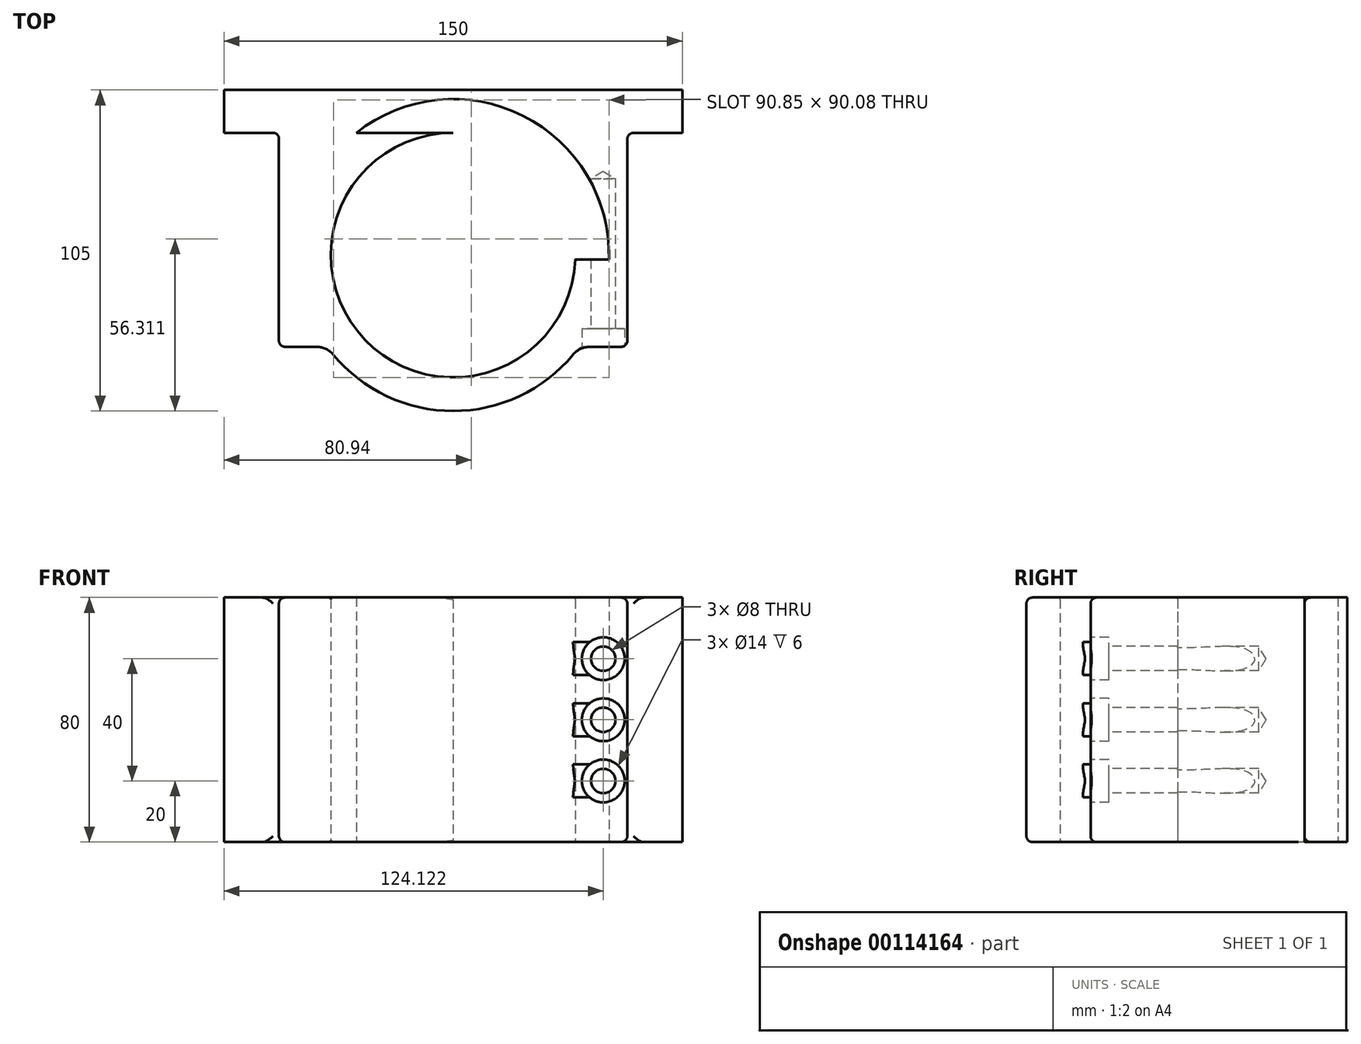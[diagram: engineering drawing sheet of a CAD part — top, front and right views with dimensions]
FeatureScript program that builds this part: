
annotation { "Feature Type Name" : "Feature", "Feature Type Description" : "" }
export const myFeature = defineFeature(function(context is Context, id is Id, definition is map)
    precondition{}
    {
        {
            var Q0;
            Q0=qCreatedBy(makeId("Top.planeOp"),FACE);
            var sketch = newSketch(context, id + "F0", { "sketchPlane" : qUnion([Q0])});
            skCircle(sketch, "E0", {"center": v(0, -54) * mm, "radius": 40 * mm});
            skCircle(sketch, "E1", {"center": v(0, -54) * mm, "radius": 51 * mm});
            skLineSegment(sketch, "E2", {"start": v(0, 0) * mm, "end": v(0, -54) * mm, "construction": true});
            skLineSegment(sketch, "E3", {"start": v(0, -54) * mm, "end": v(40, -54) * mm, "construction": true});
            skLineSegment(sketch, "E4", {"start": v(40, -54) * mm, "end": v(51, -54) * mm, "construction": true});
            skLineSegment(sketch, "E5.bottom", {"start": v(75, -14) * mm, "end": v(-75, -14) * mm});
            skLineSegment(sketch, "E5.top", {"start": v(75, 0) * mm, "end": v(-75, 0) * mm});
            skLineSegment(sketch, "E5.left", {"start": v(75, -14) * mm, "end": v(75, 0) * mm});
            skLineSegment(sketch, "E5.right", {"start": v(-75, -14) * mm, "end": v(-75, 0) * mm});
            skPoint(sketch, "E5.middle", {"position": v(0, -7) * mm});
            skLineSegment(sketch, "E6.bottom", {"start": v(57, -84) * mm, "end": v(-57, -84) * mm});
            skLineSegment(sketch, "E6.top", {"start": v(57, -14) * mm, "end": v(-57, -14) * mm});
            skLineSegment(sketch, "E6.left", {"start": v(57, -84) * mm, "end": v(57, -14) * mm});
            skLineSegment(sketch, "E6.right", {"start": v(-57, -84) * mm, "end": v(-57, -14) * mm});
            skPoint(sketch, "E6.middle", {"position": v(0, -49) * mm});
            skLineSegment(sketch, "E7.bottom", {"start": v(57, -55.5) * mm, "end": v(34, -55.5) * mm});
            skLineSegment(sketch, "E7.top", {"start": v(57, -52.5) * mm, "end": v(34, -52.5) * mm});
            skLineSegment(sketch, "E7.left", {"start": v(57, -55.5) * mm, "end": v(57, -52.5) * mm});
            skLineSegment(sketch, "E7.right", {"start": v(34, -55.5) * mm, "end": v(34, -52.5) * mm});
            skPoint(sketch, "E7.middle", {"position": v(45.5, -54) * mm});
            skLineSegment(sketch, "E8", {"start": v(0, -54) * mm, "end": v(0, -105) * mm, "construction": true});
            skSolve(sketch);
        }
        {
            var Q0;
            {var subQ0=sQuery(id+"F0.wireOp",EDGE,"E5.right");Q0=makeQuery(id+"F0.imprint","IMPRINT",FACE,{"disambiguationData":[TD([[makeQuery(id+"F0.imprint","IMPRINT",EDGE,{"derivedFrom":subQ0}),-1.0]])]});}
            var Q1;
            {var subQ5=sQuery(id+"F0.wireOp",EDGE,"E6.right");Q1=makeQuery(id+"F0.imprint","IMPRINT",FACE,{"disambiguationData":[TD([[makeQuery(id+"F0.imprint","IMPRINT",EDGE,{"derivedFrom":subQ5}),-1.0]])]});}
            var Q2;
            {var subQ0=sQuery(id+"F0.wireOp",EDGE,"E6.top");var subQ1=sQuery(id+"F0.wireOp",EDGE,"E0");var subQ7=makeQuery(id+"F0.imprint","INTERSECT",VERTEX,{"disambiguationData":[OD(0.0)],"derivedFrom":[subQ1,subQ0]});Q2=makeQuery(id+"F0.imprint","IMPRINT",FACE,{"disambiguationData":[TD([[makeQuery(id+"F0.imprint","IMPRINT",EDGE,{"disambiguationData":[TD([[subQ7,1.0]])],"derivedFrom":subQ1}),-1.0]])]});}
            var Q3;
            {var subQ0=sQuery(id+"F0.wireOp",EDGE,"E6.top");var subQ1=sQuery(id+"F0.wireOp",EDGE,"E0");var subQ2=makeQuery(id+"F0.imprint","INTERSECT",VERTEX,{"disambiguationData":[OD(0.0)],"derivedFrom":[subQ1,subQ0]});Q3=makeQuery(id+"F0.imprint","IMPRINT",FACE,{"disambiguationData":[TD([[makeQuery(id+"F0.imprint","IMPRINT",EDGE,{"disambiguationData":[TD([[subQ2,-1.0]])],"derivedFrom":subQ1}),-1.0]])]});}
            var Q4;
            {var subQ0=sQuery(id+"F0.wireOp",EDGE,"E5.left");Q4=makeQuery(id+"F0.imprint","IMPRINT",FACE,{"disambiguationData":[TD([[makeQuery(id+"F0.imprint","IMPRINT",EDGE,{"derivedFrom":subQ0}),1.0]])]});}
            var Q5;
            {var subQ5=sQuery(id+"F0.wireOp",EDGE,"E6.left");Q5=makeQuery(id+"F0.imprint","IMPRINT",FACE,{"disambiguationData":[TD([[makeQuery(id+"F0.imprint","IMPRINT",EDGE,{"derivedFrom":subQ5}),1.0]])]});}
            var Q6;
            {var subQ0=sQuery(id+"F0.wireOp",EDGE,"E6.top");var subQ1=sQuery(id+"F0.wireOp",EDGE,"E0");var subQ2=makeQuery(id+"F0.imprint","INTERSECT",VERTEX,{"disambiguationData":[OD(1.0)],"derivedFrom":[subQ1,subQ0]});Q6=makeQuery(id+"F0.imprint","IMPRINT",FACE,{"disambiguationData":[TD([[makeQuery(id+"F0.imprint","IMPRINT",EDGE,{"disambiguationData":[TD([[subQ2,1.0]])],"derivedFrom":subQ1}),-1.0]])]});}
            var Q7;
            {var subQ0=sQuery(id+"F0.wireOp",EDGE,"E6.bottom");var subQ1=sQuery(id+"F0.wireOp",EDGE,"E0");var subQ2=makeQuery(id+"F0.imprint","INTERSECT",VERTEX,{"disambiguationData":[OD(0.0)],"derivedFrom":[subQ1,subQ0]});Q7=makeQuery(id+"F0.imprint","IMPRINT",FACE,{"disambiguationData":[TD([[makeQuery(id+"F0.imprint","IMPRINT",EDGE,{"disambiguationData":[TD([[subQ2,-1.0]])],"derivedFrom":subQ1}),-1.0]])]});}
            var Q8;
            {var subQ0=sQuery(id+"F0.wireOp",EDGE,"E6.bottom");var subQ1=sQuery(id+"F0.wireOp",EDGE,"E0");var subQ2=makeQuery(id+"F0.imprint","INTERSECT",VERTEX,{"disambiguationData":[OD(1.0)],"derivedFrom":[subQ1,subQ0]});Q8=makeQuery(id+"F0.imprint","IMPRINT",FACE,{"disambiguationData":[TD([[makeQuery(id+"F0.imprint","IMPRINT",EDGE,{"disambiguationData":[TD([[subQ2,-1.0]])],"derivedFrom":subQ1}),-1.0]])]});}
            var Q9;
            {var subQ0=sQuery(id+"F0.wireOp",EDGE,"E6.top");var subQ1=sQuery(id+"F0.wireOp",EDGE,"E0");var subQ2=makeQuery(id+"F0.imprint","INTERSECT",VERTEX,{"disambiguationData":[OD(1.0)],"derivedFrom":[subQ1,subQ0]});Q9=makeQuery(id+"F0.imprint","IMPRINT",FACE,{"disambiguationData":[TD([[makeQuery(id+"F0.imprint","IMPRINT",EDGE,{"disambiguationData":[TD([[subQ2,-1.0]])],"derivedFrom":subQ1}),-1.0]])]});}
            var Q10;
            {var subQ0=sQuery(id+"F0.wireOp",EDGE,"E6.top");var subQ1=sQuery(id+"F0.wireOp",EDGE,"E1");var subQ2=makeQuery(id+"F0.imprint","INTERSECT",VERTEX,{"disambiguationData":[OD(0.0)],"derivedFrom":[subQ1,subQ0]});Q10=makeQuery(id+"F0.imprint","IMPRINT",FACE,{"disambiguationData":[TD([[makeQuery(id+"F0.imprint","IMPRINT",EDGE,{"disambiguationData":[TD([[subQ2,-1.0]])],"derivedFrom":subQ1}),1.0]])]});}
            extrude(context, id + "F1", {"entities" : qUnion([Q0, Q1, Q2, Q3, Q4, Q5, Q6, Q7, Q8, Q9, Q10]), "depth" : 80 * mm});
        }
        {
            var Q0;
            {var subQ0=sQuery(id+"F0.wireOp",EDGE,"E6.bottom");Q0=makeQuery(id+"F1.opExtrude","SWEPT_FACE",FACE,{"disambiguationData":[OSD([subQ0]),TDD([makeQuery(id+"F0.imprint","IMPRINT",EDGE,{"disambiguationData":[TD([[makeQuery(id+"F0.imprint","INTERSECT",VERTEX,{"derivedFrom":[subQ0,sQuery(id+"F0.wireOp",EDGE,"E6.left")]}),-1.0]])],"derivedFrom":subQ0})])]});}
            var sketch = newSketch(context, id + "F2", { "sketchPlane" : qUnion([Q0])});
            skLineSegment(sketch, "E9", {"start": v(49.12, 0) * mm, "end": v(49.12, 20) * mm, "construction": true});
            skLineSegment(sketch, "E10", {"start": v(49.12, 20) * mm, "end": v(49.12, 40) * mm, "construction": true});
            skPoint(sketch, "E10.endSnap0", {"position": v(57, 40) * mm});
            skLineSegment(sketch, "E11", {"start": v(49.12, 40) * mm, "end": v(49.12, 60) * mm, "construction": true});
            skLineSegment(sketch, "E12", {"start": v(49.12, 60) * mm, "end": v(49.12, 80) * mm, "construction": true});
            skSolve(sketch);
        }
        {
            var Q0;
            Q0=sQuery(id+"F2.wireOp",VERTEX,"E10.start");
            var Q1;
            Q1=sQuery(id+"F2.wireOp",VERTEX,"E11.start");
            var Q2;
            Q2=sQuery(id+"F2.wireOp",VERTEX,"E12.start");
            var Q3;
            Q3=makeQuery(id+"F1.opExtrude","SWEPT_BODY",BODY,{"disambiguationData":[OSD([sQuery(id+"F0.wireOp",EDGE,"E0"),sQuery(id+"F0.wireOp",EDGE,"E1"),sQuery(id+"F0.wireOp",EDGE,"E5.bottom"),sQuery(id+"F0.wireOp",EDGE,"E5.top"),sQuery(id+"F0.wireOp",EDGE,"E5.left"),sQuery(id+"F0.wireOp",EDGE,"E5.right"),sQuery(id+"F0.wireOp",EDGE,"E6.bottom"),sQuery(id+"F0.wireOp",EDGE,"E6.left"),sQuery(id+"F0.wireOp",EDGE,"E6.right"),sQuery(id+"F0.wireOp",EDGE,"E7.bottom"),sQuery(id+"F0.wireOp",EDGE,"E7.top")])]});
            hole(context, id + "F3", {"style" : HoleStyle.C_BORE, "endStyle" : HoleEndStyle.BLIND, "holeDiameter" : 8 * mm, "cBoreDiameter" : 14 * mm, "cBoreDepth" : 6 * mm, "holeDepth" : 55 * mm, "locations" : qUnion([Q0, Q1, Q2]), "scope" : qUnion([Q3])});
        }
        {
            var Q0;
            Q0=makeQuery(id+"F1.opExtrude","CAP_EDGE",EDGE,{"disambiguationData":[OSD([sQuery(id+"F0.wireOp",EDGE,"E0")])],"isStart":true});
            var Q1;
            Q1=makeQuery(id+"F1.opExtrude","CAP_EDGE",EDGE,{"disambiguationData":[OSD([sQuery(id+"F0.wireOp",EDGE,"E0")])],"isStart":false});
            fillet(context, id + "F4", {"entities" : qUnion([Q0, Q1]), "radius" : .6 * mm, "tangentPropagation" : true, "allowEdgeOverflow" : false});
        }
        {
            var Q0;
            {var subQ0=sQuery(id+"F0.wireOp",EDGE,"E6.bottom");var subQ1=sQuery(id+"F0.wireOp",EDGE,"E1");Q0=makeQuery(id+"F1.opExtrude","SWEPT_EDGE",EDGE,{"disambiguationData":[OSD([subQ1,subQ0]),TDD([makeQuery(id+"F0.imprint","INTERSECT",VERTEX,{"disambiguationData":[OD(1.0)],"derivedFrom":[subQ1,subQ0]})])]});}
            var Q1;
            {var subQ0=sQuery(id+"F0.wireOp",EDGE,"E6.bottom");var subQ1=sQuery(id+"F0.wireOp",EDGE,"E1");Q1=makeQuery(id+"F1.opExtrude","SWEPT_EDGE",EDGE,{"disambiguationData":[OSD([subQ1,subQ0]),TDD([makeQuery(id+"F0.imprint","INTERSECT",VERTEX,{"disambiguationData":[OD(0.0)],"derivedFrom":[subQ1,subQ0]})])]});}
            fillet(context, id + "F5", {"entities" : qUnion([Q0, Q1]), "radius" : 7 * mm, "tangentPropagation" : true, "allowEdgeOverflow" : false});
        }
        {
            var Q0;
            {var subQ0=sQuery(id+"F0.wireOp",EDGE,"E6.bottom");Q0=makeQuery(id+"F1.opExtrude","SWEPT_FACE",FACE,{"disambiguationData":[OSD([subQ0]),TDD([makeQuery(id+"F0.imprint","IMPRINT",EDGE,{"disambiguationData":[TD([[makeQuery(id+"F0.imprint","INTERSECT",VERTEX,{"derivedFrom":[subQ0,sQuery(id+"F0.wireOp",EDGE,"E6.right")]}),1.0]])],"derivedFrom":subQ0})])]});}
            var Q1;
            Q1=makeQuery(id+"F1.opExtrude","SWEPT_FACE",FACE,{"disambiguationData":[OSD([sQuery(id+"F0.wireOp",EDGE,"E6.right")])]});
            var Q2;
            Q2=makeQuery(id+"F1.opExtrude","SWEPT_EDGE",EDGE,{"disambiguationData":[OSD([sQuery(id+"F0.wireOp",EDGE,"E6.bottom"),sQuery(id+"F0.wireOp",EDGE,"E6.left")])]});
            var Q3;
            {var subQ0=sQuery(id+"F0.wireOp",EDGE,"E6.left");Q3=makeQuery(id+"F1.opExtrude","CAP_EDGE",EDGE,{"disambiguationData":[OSD([subQ0]),TDD([makeQuery(id+"F0.imprint","IMPRINT",EDGE,{"disambiguationData":[TD([[makeQuery(id+"F0.imprint","INTERSECT",VERTEX,{"derivedFrom":[sQuery(id+"F0.wireOp",EDGE,"E6.bottom"),subQ0]}),-1.0]])],"derivedFrom":subQ0})])],"isStart":true});}
            var Q4;
            {var subQ0=sQuery(id+"F0.wireOp",EDGE,"E6.left");Q4=makeQuery(id+"F1.opExtrude","CAP_EDGE",EDGE,{"disambiguationData":[OSD([subQ0]),TDD([makeQuery(id+"F0.imprint","IMPRINT",EDGE,{"disambiguationData":[TD([[makeQuery(id+"F0.imprint","INTERSECT",VERTEX,{"derivedFrom":[sQuery(id+"F0.wireOp",EDGE,"E6.bottom"),subQ0]}),-1.0]])],"derivedFrom":subQ0})])],"isStart":false});}
            var Q5;
            {var subQ0=sQuery(id+"F0.wireOp",EDGE,"E6.left");Q5=makeQuery(id+"F1.opExtrude","CAP_EDGE",EDGE,{"disambiguationData":[OSD([subQ0]),TDD([makeQuery(id+"F0.imprint","IMPRINT",EDGE,{"disambiguationData":[TD([[makeQuery(id+"F0.imprint","INTERSECT",VERTEX,{"derivedFrom":[sQuery(id+"F0.wireOp",EDGE,"E5.bottom"),sQuery(id+"F0.wireOp",EDGE,"E6.top"),subQ0]}),1.0]])],"derivedFrom":subQ0})])],"isStart":true});}
            var Q6;
            {var subQ0=sQuery(id+"F0.wireOp",EDGE,"E6.left");Q6=makeQuery(id+"F1.opExtrude","CAP_EDGE",EDGE,{"disambiguationData":[OSD([subQ0]),TDD([makeQuery(id+"F0.imprint","IMPRINT",EDGE,{"disambiguationData":[TD([[makeQuery(id+"F0.imprint","INTERSECT",VERTEX,{"derivedFrom":[sQuery(id+"F0.wireOp",EDGE,"E5.bottom"),sQuery(id+"F0.wireOp",EDGE,"E6.top"),subQ0]}),1.0]])],"derivedFrom":subQ0})])],"isStart":false});}
            var Q7;
            Q7=makeQuery(id+"F1.opExtrude","SWEPT_EDGE",EDGE,{"disambiguationData":[OSD([sQuery(id+"F0.wireOp",EDGE,"E5.bottom"),sQuery(id+"F0.wireOp",EDGE,"E6.top"),sQuery(id+"F0.wireOp",EDGE,"E6.left")])]});
            fillet(context, id + "F6", {"entities" : qUnion([Q0, Q1, Q2, Q3, Q4, Q5, Q6, Q7]), "radius" : 2 * mm, "tangentPropagation" : true, "allowEdgeOverflow" : false});
        }
    });
